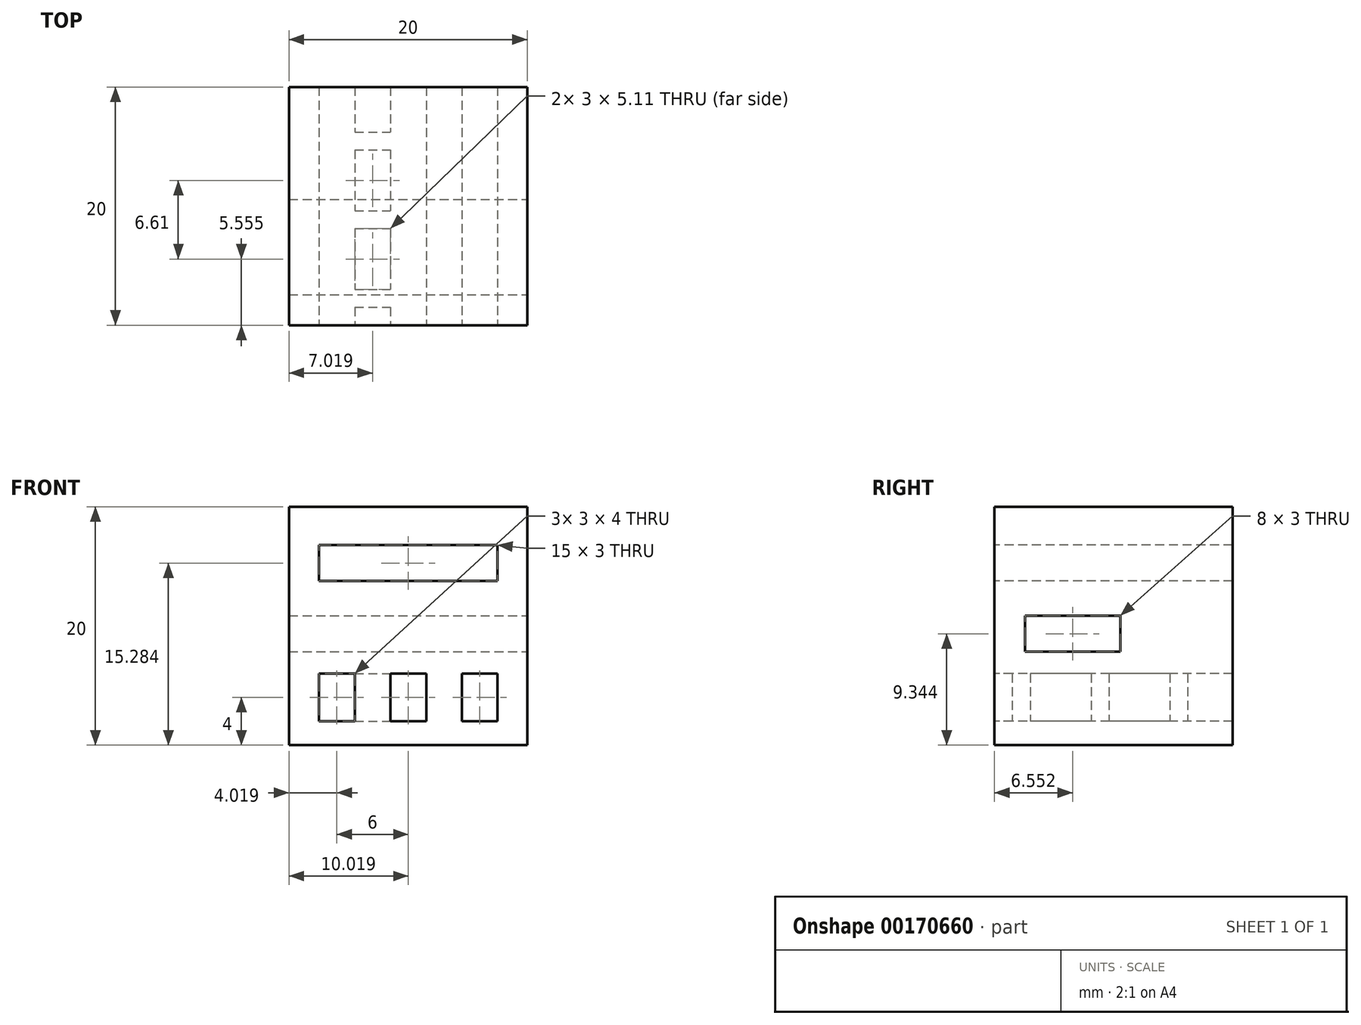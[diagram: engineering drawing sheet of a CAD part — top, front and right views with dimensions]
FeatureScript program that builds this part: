
annotation { "Feature Type Name" : "Feature", "Feature Type Description" : "" }
export const myFeature = defineFeature(function(context is Context, id is Id, definition is map)
    precondition{}
    {
        {
            var Q0;
            Q0=qCreatedBy(makeId("Top.planeOp"),FACE);
            var sketch = newSketch(context, id + "F0", { "sketchPlane" : qUnion([Q0])});
            skLineSegment(sketch, "E0.bottom", {"start": v(-10, 10) * mm, "end": v(10, 10) * mm});
            skLineSegment(sketch, "E0.top", {"start": v(-10, -10) * mm, "end": v(10, -10) * mm});
            skLineSegment(sketch, "E0.left", {"start": v(-10, 10) * mm, "end": v(-10, -10) * mm});
            skLineSegment(sketch, "E0.right", {"start": v(10, 10) * mm, "end": v(10, -10) * mm});
            skPoint(sketch, "E0.middle", {"position": v(0, 0) * mm});
            skSolve(sketch);
        }
        {
            var Q0;
            Q0 = qSketchRegion(id + "F0", true);
            extrude(context, id + "F1", {"entities" : qUnion([Q0]), "depth" : 20 * mm});
        }
        {
            var Q0;
            Q0=makeQuery(id+"F1.opExtrude","SWEPT_FACE",FACE,{"disambiguationData":[OSD([sQuery(id+"F0.wireOp",EDGE,"E0.top")])]});
            var sketch = newSketch(context, id + "F2", { "sketchPlane" : qUnion([Q0])});
            skLineSegment(sketch, "E1.bottom", {"start": v(-7.48, 6) * mm, "end": v(-4.48, 6) * mm});
            skLineSegment(sketch, "E1.top", {"start": v(-7.48, 2) * mm, "end": v(-4.48, 2) * mm});
            skLineSegment(sketch, "E1.left", {"start": v(-7.48, 6) * mm, "end": v(-7.48, 2) * mm});
            skLineSegment(sketch, "E1.right", {"start": v(-4.48, 6) * mm, "end": v(-4.48, 2) * mm});
            skLineSegment(sketch, "E2.1.0.0", {"start": v(-1.48, 6) * mm, "end": v(1.52, 6) * mm});
            skLineSegment(sketch, "E2.1.0.1", {"start": v(-1.48, 2) * mm, "end": v(1.52, 2) * mm});
            skLineSegment(sketch, "E2.1.0.2", {"start": v(-1.48, 6) * mm, "end": v(-1.48, 2) * mm});
            skLineSegment(sketch, "E2.1.0.3", {"start": v(1.52, 6) * mm, "end": v(1.52, 2) * mm});
            skLineSegment(sketch, "E2.2.0.0", {"start": v(4.52, 6) * mm, "end": v(7.52, 6) * mm});
            skLineSegment(sketch, "E2.2.0.1", {"start": v(4.52, 2) * mm, "end": v(7.52, 2) * mm});
            skLineSegment(sketch, "E2.2.0.2", {"start": v(4.52, 6) * mm, "end": v(4.52, 2) * mm});
            skLineSegment(sketch, "E2.2.0.3", {"start": v(7.52, 6) * mm, "end": v(7.52, 2) * mm});
            skLineSegment(sketch, "E2.direction1", {"start": v(-7.48, 2) * mm, "end": v(-1.48, 2) * mm, "construction": true});
            skLineSegment(sketch, "E3.bottom", {"start": v(-7.48, 16.78) * mm, "end": v(7.52, 16.78) * mm});
            skLineSegment(sketch, "E3.top", {"start": v(-7.48, 13.78) * mm, "end": v(7.52, 13.78) * mm});
            skLineSegment(sketch, "E3.left", {"start": v(-7.48, 16.78) * mm, "end": v(-7.48, 13.78) * mm});
            skLineSegment(sketch, "E3.right", {"start": v(7.52, 16.78) * mm, "end": v(7.52, 13.78) * mm});
            skSolve(sketch);
        }
        {
            var Q0;
            Q0 = qSketchRegion(id + "F2", true);
            extrude(context, id + "F3", {"entities" : qUnion([Q0]), "operationType" : NewBodyOperationType.REMOVE, "endBound" : BoundingType.THROUGH_ALL, "oppositeDirection" : true, "depth" : 25 * mm});
        }
        {
            var Q0;
            Q0=makeQuery(id+"F1.opExtrude","SWEPT_FACE",FACE,{"disambiguationData":[OSD([sQuery(id+"F0.wireOp",EDGE,"E0.right")])]});
            var sketch = newSketch(context, id + "F4", { "sketchPlane" : qUnion([Q0])});
            skLineSegment(sketch, "E4.bottom", {"start": v(-7.45, 10.84) * mm, "end": v(0.55, 10.84) * mm});
            skLineSegment(sketch, "E4.top", {"start": v(-7.45, 7.84) * mm, "end": v(0.55, 7.84) * mm});
            skLineSegment(sketch, "E4.left", {"start": v(-7.45, 10.84) * mm, "end": v(-7.45, 7.84) * mm});
            skLineSegment(sketch, "E4.right", {"start": v(0.55, 10.84) * mm, "end": v(0.55, 7.84) * mm});
            skSolve(sketch);
        }
        {
            var Q0;
            Q0 = qSketchRegion(id + "F4", true);
            extrude(context, id + "F5", {"entities" : qUnion([Q0]), "operationType" : NewBodyOperationType.REMOVE, "endBound" : BoundingType.THROUGH_ALL, "oppositeDirection" : true, "depth" : 25 * mm});
        }
        {
            var Q0;
            Q0=makeQuery(id+"F3.boolean.opBoolean","COPY",FACE,{"derivedFrom":makeQuery(id+"F3.opExtrude","SWEPT_FACE",FACE,{"disambiguationData":[OSD([sQuery(id+"F2.wireOp",EDGE,"E2.1.0.2")])]})});
            var sketch = newSketch(context, id + "F6", { "sketchPlane" : qUnion([Q0])});
            skLineSegment(sketch, "E5.bottom", {"start": v(-8.5, 6) * mm, "end": v(-7, 6) * mm});
            skLineSegment(sketch, "E5.top", {"start": v(-8.5, 2) * mm, "end": v(-7, 2) * mm});
            skLineSegment(sketch, "E5.left", {"start": v(-8.5, 6) * mm, "end": v(-8.5, 2) * mm});
            skLineSegment(sketch, "E5.right", {"start": v(-7, 6) * mm, "end": v(-7, 2) * mm});
            skLineSegment(sketch, "E6.1.0.0", {"start": v(-1.9, 6) * mm, "end": v(-1.89, 2) * mm});
            skLineSegment(sketch, "E6.1.0.1", {"start": v(-0.4, 6) * mm, "end": v(-0.4, 2) * mm});
            skLineSegment(sketch, "E6.1.0.2", {"start": v(-1.9, 6) * mm, "end": v(-0.4, 6) * mm});
            skLineSegment(sketch, "E6.1.0.3", {"start": v(-1.9, 2) * mm, "end": v(-0.4, 2) * mm});
            skLineSegment(sketch, "E6.2.0.0", {"start": v(4.72, 6) * mm, "end": v(4.72, 2) * mm});
            skLineSegment(sketch, "E6.2.0.1", {"start": v(6.22, 6) * mm, "end": v(6.22, 2) * mm});
            skLineSegment(sketch, "E6.2.0.2", {"start": v(4.72, 6) * mm, "end": v(6.22, 6) * mm});
            skLineSegment(sketch, "E6.2.0.3", {"start": v(4.72, 2) * mm, "end": v(6.22, 2) * mm});
            skLineSegment(sketch, "E6.direction1", {"start": v(-8.5, 2) * mm, "end": v(-1.9, 2) * mm, "construction": true});
            skSolve(sketch);
        }
        {
            var Q0;
            Q0 = qSketchRegion(id + "F6", true);
            extrude(context, id + "F7", {"entities" : qUnion([Q0]), "operationType" : NewBodyOperationType.REMOVE, "endBound" : BoundingType.UP_TO_NEXT, "oppositeDirection" : true, "depth" : 25 * mm});
        }
    });
